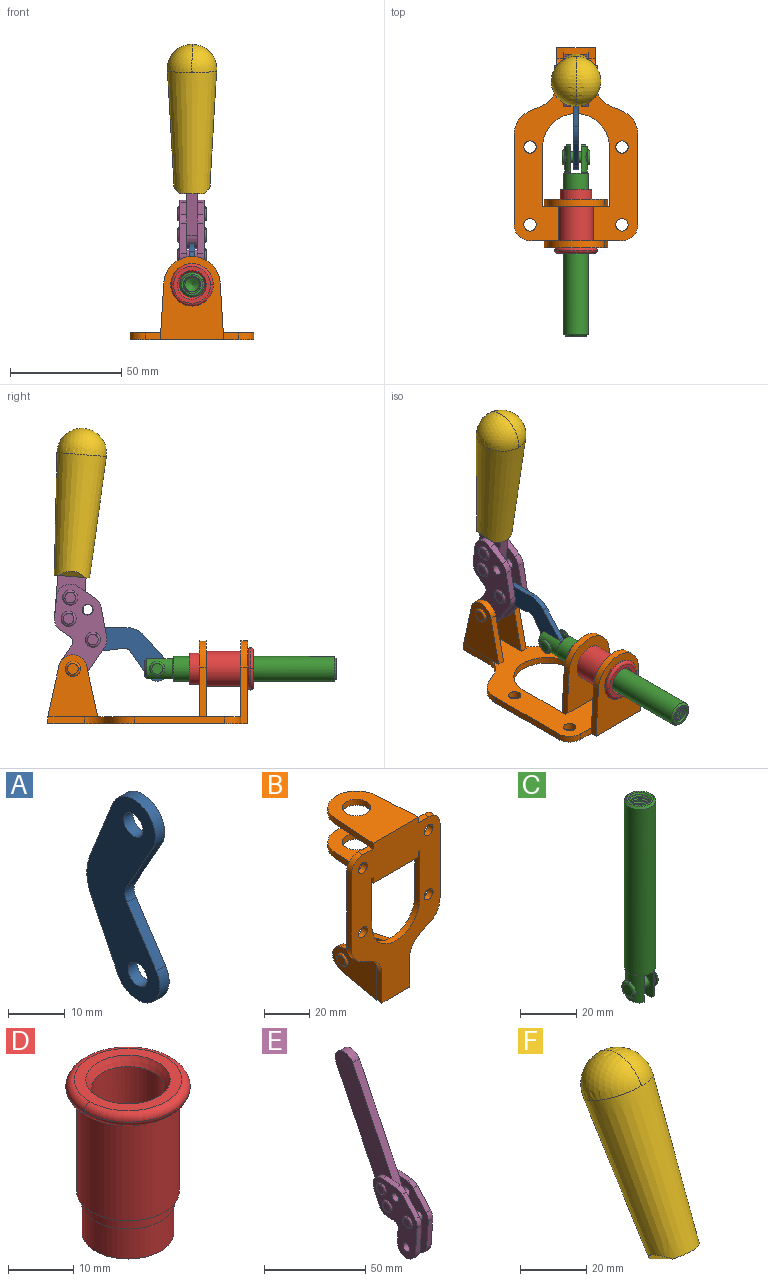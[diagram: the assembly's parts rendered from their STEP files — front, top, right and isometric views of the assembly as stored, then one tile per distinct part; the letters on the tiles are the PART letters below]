
ASSEMBLY  parts=6 mates=6
PART A: 12 faces, bbox 2.3x18.2x42.8 mm
  f0: cylinder r=2.4mm len=4.8mm, axis (1,0,0), area 34.9mm2, adj f4,f11
  f1: cylinder r=10.41mm len=8.47mm, axis (1,0,0), area 20.2mm2, adj f4,f9,f10,f11
  f2: cylinder r=3.05mm len=3.16mm, axis (1,0,0), area 7.7mm2, adj f4,f6,f7,f11
  f3: cylinder r=2.4mm len=4.8mm, axis (1,0,0), area 34.9mm2, adj f4,f11
  f4: plane 42.81x18.23mm, normal (-1,0,0), area 414.1mm2, adj f0,f1,f2,f3,f5,f6,f7,f8
  f5: cylinder r=5.54mm len=10.67mm, axis (1,0,0), area 41.8mm2, adj f4,f6,f10,f11
  f6: plane 11.66x6.53mm, normal (0,-0.87,-0.49), area 30.9mm2, adj f2,f4,f5,f11
  f7: plane 11.17x7.33mm, normal (0,-0.84,0.55), area 30.9mm2, adj f2,f4,f8,f11
  f8: cylinder r=5.54mm len=10.51mm, axis (1,0,0), area 41.8mm2, adj f4,f7,f9,f11
  f9: plane 13.67x6.67mm, normal (0,0.9,-0.44), area 35.1mm2, adj f1,f4,f8,f11
  f10: plane 14.1x5.7mm, normal (0,0.93,0.37), area 35.1mm2, adj f1,f4,f5,f11
  f11: plane 42.81x18.23mm, normal (1,0,0), area 414.1mm2, adj f0,f1,f2,f3,f5,f6,f7,f8
PART B: 55 faces, bbox 55.7x37.4x89.8 mm
  f0: torus R=2.41mm, axis (-1,0,0), area 15mm2, adj f11,f15,f25
  f1: torus R=2.41mm, axis (-1,0,0), area 15mm2, adj f10,f12,f22
  f2: cylinder r=2.78mm len=5.56mm, axis (0,-1,0), area 54.2mm2, adj f30,f54
  f3: cylinder r=14.99mm len=29.97mm, axis (0,-1,0), area 145.9mm2, adj f30,f49,f53,f54
  f4: cylinder r=2.78mm len=5.56mm, axis (0,-1,0), area 54.2mm2, adj f30,f54
  f5: cylinder r=2.78mm len=5.56mm, axis (0,-1,0), area 54.2mm2, adj f30,f54
  f6: cylinder r=2.78mm len=5.56mm, axis (0,-1,0), area 54.2mm2, adj f30,f54
  f7: cylinder r=6.35mm len=12.7mm, axis (0,0,1), area 123.6mm2, adj f27,f51
  f8: cylinder r=6.35mm len=12.7mm, axis (0,0,-1), area 124.7mm2, adj f21,f35
  f9: cylinder r=2.41mm len=11.18mm, axis (-1,0,0), area 169.4mm2, adj f16,f19
  f10: plane 4.83x4.83mm, normal (1,0,0), area 18.3mm2, adj f1,f12
  f11: plane 4.83x4.83mm, normal (-1,0,0), area 18.3mm2, adj f0,f15
  f12: torus R=2.41mm, axis (-1,0,0), area 15mm2, adj f1,f10,f22
  f13: cylinder r=6.35mm len=12.41mm, axis (1,0,0), area 53.4mm2, adj f18,f19,f22,f23
  f14: cylinder r=6.35mm len=12.41mm, axis (-1,0,0), area 53.4mm2, adj f16,f17,f24,f25
  f15: torus R=2.41mm, axis (-1,0,0), area 15mm2, adj f0,f11,f25
  f16: plane 27.86x22.35mm, normal (1,0,0), area 425.4mm2, adj f9,f14,f17,f24,f30
  f17: plane 22.86x4.97mm, normal (0,0.21,0.98), area 72.5mm2, adj f14,f16,f25,f30
  f18: plane 22.86x4.97mm, normal (0,0.21,0.98), area 72.5mm2, adj f13,f19,f22,f30
  f19: plane 27.86x22.35mm, normal (-1,0,0), area 425.4mm2, adj f9,f13,f18,f23,f30
  f20: cylinder r=12.7mm len=25.35mm, axis (0,0,-1), area 119.8mm2, adj f21,f34,f35,f36
  f21: plane 34.21x28.07mm, normal (0,0,-1), area 702.4mm2, adj f8,f20,f30,f34,f36
  f22: plane 27.96x22.45mm, normal (1,0,0), area 407.2mm2, adj f1,f12,f13,f18,f23,f30,f42,f43
  f23: plane 22.86x4.97mm, normal (0,0.21,-0.98), area 72.5mm2, adj f13,f19,f22,f44
  f24: plane 22.86x4.97mm, normal (0,0.21,-0.98), area 72.5mm2, adj f14,f16,f25,f44
  f25: plane 27.86x22.35mm, normal (-1,0,0), area 407.1mm2, adj f0,f14,f15,f17,f24,f30,f45,f46
  f26: plane 3.1x0.95mm, normal (0,0,-1), area 2.7mm2, adj f30,f49,f50,f54
  f27: plane 34.21x28.07mm, normal (0,0,1), area 702.4mm2, adj f7,f28,f30,f50,f52
  f28: cylinder r=12.7mm len=25.35mm, axis (0,0,1), area 118.8mm2, adj f27,f50,f51,f52
  f29: plane 3.1x0.95mm, normal (0,0,-1), area 2.7mm2, adj f30,f52,f53,f54
  f30: plane 86.54x55.63mm, normal (0,1,0), area 2362.9mm2, adj f2,f3,f4,f5,f6,f16,f17,f18
  f31: plane 40.56x3.1mm, normal (-1,0,0), area 125.7mm2, adj f30,f32,f48,f54
  f32: cylinder r=7.11mm len=7.11mm, axis (0,-1,0), area 34.6mm2, adj f30,f31,f33,f54
  f33: plane 6.67x3.1mm, normal (0,0,1), area 20.4mm2, adj f30,f32,f34,f54
  f34: plane 25.39x3.13mm, normal (-1,0.06,0), area 79.5mm2, adj f20,f21,f33,f35,f54
  f35: plane 37.31x28.45mm, normal (0,0,1), area 789.9mm2, adj f8,f20,f34,f36,f54
  f36: plane 25.39x3.13mm, normal (1,0.06,0), area 79.5mm2, adj f20,f21,f35,f37,f54
  f37: plane 6.67x3.1mm, normal (0,0,1), area 20.4mm2, adj f30,f36,f38,f54
  f38: cylinder r=7.11mm len=7.11mm, axis (0,-1,0), area 34.6mm2, adj f30,f37,f39,f54
  f39: plane 40.56x3.1mm, normal (1,0,0), area 125.7mm2, adj f30,f38,f40,f54
  f40: cylinder r=11.18mm len=10.16mm, axis (0,-1,0), area 39.5mm2, adj f30,f39,f41,f54
  f41: plane 6.09x3.1mm, normal (0.42,0,-0.91), area 20.8mm2, adj f30,f40,f42,f54
  f42: cylinder r=11.18mm len=9.41mm, axis (0,-1,0), area 37.2mm2, adj f22,f30,f41,f43,f54
  f43: plane 16.5x3.1mm, normal (1,0,0), area 51.1mm2, adj f22,f42,f44,f54
  f44: plane 17.37x3.1mm, normal (0,0,-1), area 53.8mm2, adj f23,f24,f30,f43,f45,f54
  f45: plane 16.5x3.1mm, normal (-1,0,0), area 51.1mm2, adj f25,f44,f46,f54
  f46: cylinder r=11.18mm len=9.41mm, axis (0,-1,0), area 37.2mm2, adj f25,f30,f45,f47,f54
  f47: plane 6.09x3.1mm, normal (-0.42,0,-0.91), area 20.8mm2, adj f30,f46,f48,f54
  f48: cylinder r=11.18mm len=10.16mm, axis (0,-1,0), area 39.5mm2, adj f30,f31,f47,f54
  f49: plane 26.54x3.1mm, normal (-1,0,0), area 82.3mm2, adj f3,f26,f30,f54
  f50: plane 25.39x3.1mm, normal (1,0.06,0), area 78.8mm2, adj f26,f27,f28,f51,f54
  f51: plane 37.31x28.45mm, normal (0,0,-1), area 789.9mm2, adj f7,f28,f50,f52,f54
  f52: plane 25.39x3.1mm, normal (-1,0.06,0), area 78.8mm2, adj f27,f28,f29,f51,f54
  f53: plane 26.54x3.1mm, normal (1,0,0), area 82.3mm2, adj f3,f29,f30,f54
  f54: plane 89.66x55.63mm, normal (0,-1,0), area 2678.5mm2, adj f2,f3,f4,f5,f6,f26,f29,f31
PART C: 48 faces, bbox 12.6x11.1x86.1 mm
  f0: torus R=2.41mm, axis (-1,0,0), area 15mm2, adj f30,f32,f34
  f1: torus R=2.41mm, axis (-1,0,0), area 15mm2, adj f29,f31,f33
  f2: cylinder r=5.54mm len=72.39mm, axis (0,0,1), area 2518.5mm2, adj f3,f4,f42,f43
  f3: cone r=5.54mm half-angle=45deg, axis (0,0,1), area 7.6mm2, adj f2,f5,f41
  f4: cone r=5.54mm half-angle=45deg, axis (0,0,-1), area 34.9mm2, adj f2,f39
  f5: cylinder r=5.08mm len=11.48mm, axis (0,0,1), area 108.3mm2, adj f3,f7,f8,f41
  f6: cylinder r=2.41mm len=4.83mm, axis (-1,0,0), area 71.2mm2, adj f40,f41
  f7: cylinder r=2.41mm len=4.83mm, axis (-1,0,0), area 7.6mm2, adj f5,f34
  f8: cone r=5.08mm half-angle=45deg, axis (0,0,1), area 10.6mm2, adj f5,f37,f41
  f9: cone r=3.98mm half-angle=45deg, axis (0,0,1), area 17.6mm2, adj f27,f39,f45,f46,f47
  f10: cylinder r=2.41mm len=4.83mm, axis (-1,0,0), area 7.6mm2, adj f33,f38
  f11: cylinder r=3.2mm len=6.4mm, axis (0,0,1), area 78.4mm2, adj f12,f28,f44,f45,f47
  f12: cylinder r=3.2mm len=6.4mm, axis (0,0,1), area 10.5mm2, adj f11,f13,f45,f47
  f13: cylinder r=3.2mm len=6.4mm, axis (0,0,1), area 10.5mm2, adj f12,f14,f45,f47
  f14: cylinder r=3.2mm len=6.4mm, axis (0,0,1), area 10.5mm2, adj f13,f15,f45,f47
  f15: cylinder r=3.2mm len=6.4mm, axis (0,0,1), area 10.5mm2, adj f14,f16,f45,f47
  f16: cylinder r=3.2mm len=6.4mm, axis (0,0,1), area 10.5mm2, adj f15,f17,f45,f47
  f17: cylinder r=3.2mm len=6.4mm, axis (0,0,1), area 10.5mm2, adj f16,f18,f45,f47
  f18: cylinder r=3.2mm len=6.4mm, axis (0,0,1), area 10.5mm2, adj f17,f19,f45,f47
  f19: cylinder r=3.2mm len=6.4mm, axis (0,0,1), area 10.5mm2, adj f18,f20,f45,f47
  f20: cylinder r=3.2mm len=6.4mm, axis (0,0,1), area 10.5mm2, adj f19,f21,f45,f47
  f21: cylinder r=3.2mm len=6.4mm, axis (0,0,1), area 10.5mm2, adj f20,f22,f45,f47
  f22: cylinder r=3.2mm len=6.4mm, axis (0,0,1), area 10.5mm2, adj f21,f23,f45,f47
  f23: cylinder r=3.2mm len=6.4mm, axis (0,0,1), area 10.5mm2, adj f22,f24,f45,f47
  f24: cylinder r=3.2mm len=6.4mm, axis (0,0,1), area 10.5mm2, adj f23,f25,f45,f47
  f25: cylinder r=3.2mm len=6.4mm, axis (0,0,1), area 10.5mm2, adj f24,f26,f45,f47
  f26: cylinder r=3.2mm len=6.4mm, axis (0,0,1), area 10.5mm2, adj f25,f27,f45,f47
  f27: cylinder r=3.2mm len=6.4mm, axis (0,0,1), area 7.4mm2, adj f9,f26,f45,f47
  f28: cone r=3.2mm half-angle=60deg, axis (0,0,1), area 37.2mm2, adj f11
  f29: plane 4.83x4.83mm, normal (-1,0,0), area 18.3mm2, adj f1,f31
  f30: plane 4.83x4.83mm, normal (1,0,0), area 18.3mm2, adj f0,f32
  f31: torus R=2.41mm, axis (-1,0,0), area 15mm2, adj f1,f29,f33
  f32: torus R=2.41mm, axis (-1,0,0), area 15mm2, adj f0,f30,f34
  f33: plane 6.83x6.83mm, normal (1,0,0), area 18.3mm2, adj f1,f10,f31
  f34: plane 6.83x6.83mm, normal (-1,0,0), area 18.3mm2, adj f0,f7,f32
  f35: cone r=5.08mm half-angle=45deg, axis (0,0,1), area 10.6mm2, adj f36,f38,f40
  f36: plane 7.25x1.97mm, normal (0,0,-1), area 10mm2, adj f35,f40
  f37: plane 7.25x1.97mm, normal (0,0,-1), area 10mm2, adj f8,f41
  f38: cylinder r=5.08mm len=11.48mm, axis (0,0,1), area 108.3mm2, adj f10,f35,f40,f42
  f39: plane 9.55x9.55mm, normal (0,0,1), area 22mm2, adj f4,f9
  f40: plane 12.76x10.09mm, normal (1,0,0), area 95.7mm2, adj f6,f35,f36,f38,f42,f43
  f41: plane 12.76x10.09mm, normal (-1,0,0), area 95.7mm2, adj f3,f5,f6,f8,f37,f43
  f42: cone r=5.54mm half-angle=45deg, axis (0,0,1), area 7.6mm2, adj f2,f38,f40
  f43: plane 11.07x4.7mm, normal (0,0,-1), area 50.4mm2, adj f2,f40,f41
  f44: plane 0.89x0.62mm, normal (-1,0,0), area 0.3mm2, adj f11,f45,f46,f47
  f45: bspline ~24.8x7.63mm, area 266.6mm2, adj f9,f11,f12,f13,f14,f15,f16,f17
  f46: bspline ~24.87x7.63mm, area 73.6mm2, adj f9,f44,f45,f47
  f47: bspline ~24.98x7.63mm, area 272.5mm2, adj f9,f11,f12,f13,f14,f15,f16,f17
PART D: 15 faces, bbox 20.6x20.6x28.7 mm
  f0: torus R=8.26mm, axis (0,0,1), area 56.8mm2, adj f1,f10,f12
  f1: torus R=8.26mm, axis (0,0,1), area 56.8mm2, adj f0,f6,f13
  f2: cylinder r=5.59mm len=25.91mm, axis (0,0,1), area 909.6mm2, adj f3,f4
  f3: cone r=6.86mm half-angle=45deg, axis (0,0,-1), area 70.2mm2, adj f2,f14
  f4: cone r=6.47mm half-angle=30deg, axis (0,0,1), area 66.7mm2, adj f2,f13
  f5: cylinder r=7.04mm len=14.07mm, axis (0,0,1), area 252.6mm2, adj f11,f14
  f6: torus R=8.26mm, axis (0,0,1), area 56.8mm2, adj f1,f12,f13
  f7: cylinder r=7.16mm len=14.33mm, axis (0,0,1), area 91.5mm2, adj f9,f11
  f8: cylinder r=7.86mm len=18.42mm, axis (0,0,1), area 909.6mm2, adj f9,f10
  f9: plane 15.72x15.72mm, normal (0,0,-1), area 33mm2, adj f7,f8
  f10: plane 16.51x16.51mm, normal (0,0,-1), area 19.9mm2, adj f0,f8,f12
  f11: plane 14.33x14.33mm, normal (0,0,-1), area 5.7mm2, adj f5,f7
  f12: torus R=8.26mm, axis (0,0,1), area 56.8mm2, adj f0,f6,f10
  f13: plane 16.51x16.51mm, normal (0,0,1), area 82.7mm2, adj f1,f4,f6
  f14: plane 14.07x14.07mm, normal (0,0,-1), area 7.8mm2, adj f3,f5
PART E: 59 faces, bbox 12.9x60.2x99.6 mm
  f0: torus R=2.39mm, axis (-1,0,0), area 14.9mm2, adj f20,f43,f51
  f1: torus R=2.39mm, axis (-1,0,0), area 14.9mm2, adj f19,f42,f51
  f2: torus R=2.39mm, axis (-1,0,0), area 14.9mm2, adj f18,f35,f51
  f3: torus R=2.39mm, axis (-1,0,0), area 14.9mm2, adj f14,f17,f23
  f4: torus R=2.39mm, axis (-1,0,0), area 14.9mm2, adj f13,f16,f23
  f5: torus R=2.39mm, axis (-1,0,0), area 14.9mm2, adj f12,f15,f23
  f6: cylinder r=2.39mm len=4.78mm, axis (1,0,0), area 46.5mm2, adj f48,f50,f51
  f7: cylinder r=2.39mm len=4.78mm, axis (1,0,0), area 46.5mm2, adj f50,f51
  f8: cylinder r=6.35mm len=12.68mm, axis (1,0,0), area 61.8mm2, adj f38,f39,f50,f51
  f9: cylinder r=2.39mm len=4.78mm, axis (-1,0,0), area 70.5mm2, adj f46,f50
  f10: cylinder r=2.39mm len=4.78mm, axis (-1,0,0), area 46.5mm2, adj f23,f45,f46
  f11: cylinder r=2.39mm len=4.78mm, axis (-1,0,0), area 46.5mm2, adj f23,f46
  f12: plane 4.78x4.78mm, normal (1,0,0), area 17.9mm2, adj f5,f15
  f13: plane 4.78x4.78mm, normal (1,0,0), area 17.9mm2, adj f4,f16
  f14: plane 4.78x4.78mm, normal (1,0,0), area 17.9mm2, adj f3,f17
  f15: torus R=2.39mm, axis (-1,0,0), area 14.9mm2, adj f5,f12,f23
  f16: torus R=2.39mm, axis (-1,0,0), area 14.9mm2, adj f4,f13,f23
  f17: torus R=2.39mm, axis (-1,0,0), area 14.9mm2, adj f3,f14,f23
  f18: plane 4.78x4.78mm, normal (-1,0,0), area 17.9mm2, adj f2,f35
  f19: plane 4.78x4.78mm, normal (-1,0,0), area 17.9mm2, adj f1,f42
  f20: plane 4.78x4.78mm, normal (-1,0,0), area 17.9mm2, adj f0,f43
  f21: plane 2.26x0.2mm, normal (1,0,0), area 0.2mm2, adj f31,f44
  f22: plane 2.26x0.2mm, normal (-1,0,0), area 0.2mm2, adj f41,f44
  f23: plane 39.37x30.77mm, normal (1,0,0), area 565.5mm2, adj f3,f4,f5,f10,f11,f15,f16,f17
  f24: cylinder r=6.1mm len=4.15mm, axis (-1,0,0), area 14.7mm2, adj f23,f25,f32,f46
  f25: plane 10.25x9.01mm, normal (0,-0.75,0.66), area 42.3mm2, adj f23,f24,f26,f46
  f26: cylinder r=6.35mm len=4.64mm, axis (-1,0,0), area 15.6mm2, adj f23,f25,f27,f46
  f27: plane 15.84x3.1mm, normal (0,-1,-0.07), area 49.2mm2, adj f23,f26,f28,f46
  f28: cylinder r=6.35mm len=12.68mm, axis (-1,0,0), area 61.8mm2, adj f23,f27,f29,f46
  f29: plane 8.11x3.1mm, normal (0,1,0.07), area 25.2mm2, adj f23,f28,f30,f46
  f30: cylinder r=3.05mm len=3.25mm, axis (-1,0,0), area 14.8mm2, adj f23,f29,f31,f46
  f31: plane 5.99x3.1mm, normal (0,0.07,-1), area 18.6mm2, adj f21,f23,f30,f44,f46
  f32: plane 9.5x3.1mm, normal (0,-0.07,1), area 29.5mm2, adj f23,f24,f33,f46,f47
  f33: cylinder r=6.1mm len=8.63mm, axis (-1,0,0), area 39.1mm2, adj f23,f32,f34,f47
  f34: plane 8.65x3.96mm, normal (0,0.91,-0.42), area 29.5mm2, adj f23,f33,f44,f47
  f35: torus R=2.39mm, axis (-1,0,0), area 14.9mm2, adj f2,f18,f51
  f36: plane 10.25x9.01mm, normal (0,-0.75,0.66), area 42.3mm2, adj f37,f49,f50,f51
  f37: cylinder r=6.35mm len=4.64mm, axis (1,0,0), area 15.6mm2, adj f36,f38,f50,f51
  f38: plane 15.84x3.1mm, normal (0,-1,-0.07), area 49.2mm2, adj f8,f37,f50,f51
  f39: plane 8.11x3.1mm, normal (0,1,0.07), area 25.2mm2, adj f8,f40,f50,f51
  f40: cylinder r=3.05mm len=3.25mm, axis (1,0,0), area 14.8mm2, adj f39,f41,f50,f51
  f41: plane 5.99x3.1mm, normal (0,0.07,-1), area 18.6mm2, adj f22,f40,f44,f50,f51
  f42: torus R=2.39mm, axis (-1,0,0), area 14.9mm2, adj f1,f19,f51
  f43: torus R=2.39mm, axis (-1,0,0), area 14.9mm2, adj f0,f20,f51
  f44: cylinder r=6.35mm len=12.12mm, axis (-1,0,0), area 128.9mm2, adj f21,f22,f23,f31,f34,f41,f46,f47
  f45: plane 2.65x1.35mm, normal (1,0,0), area 1mm2, adj f10,f55
  f46: plane 39.08x20.42mm, normal (-1,0,0), area 412.5mm2, adj f9,f10,f11,f24,f25,f26,f27,f28
  f47: plane 77.62x39.82mm, normal (1,0,0), area 850mm2, adj f32,f33,f34,f44,f53,f54,f55
  f48: plane 2.65x1.35mm, normal (-1,0,0), area 1mm2, adj f6,f55
  f49: cylinder r=6.1mm len=4.15mm, axis (1,0,0), area 14.7mm2, adj f36,f50,f51,f56
  f50: plane 39.08x20.42mm, normal (1,0,0), area 412.5mm2, adj f6,f7,f8,f9,f36,f37,f38,f39
  f51: plane 39.37x30.77mm, normal (-1,0,0), area 565.5mm2, adj f0,f1,f2,f6,f7,f8,f35,f36
  f52: plane 8.65x3.96mm, normal (0,0.91,-0.42), area 29.5mm2, adj f44,f51,f57,f58
  f53: plane 68.49x33.4mm, normal (0,0.9,-0.44), area 358.1mm2, adj f44,f47,f54,f58
  f54: cylinder r=6.35mm len=12.06mm, axis (1,0,0), area 93.7mm2, adj f47,f53,f55,f58
  f55: plane 68.49x33.4mm, normal (0,-0.9,0.44), area 358.1mm2, adj f44,f45,f46,f47,f48,f50,f54,f58
  f56: plane 9.5x3.1mm, normal (0,-0.07,1), area 29.5mm2, adj f49,f50,f51,f57,f58
  f57: cylinder r=6.1mm len=8.63mm, axis (1,0,0), area 39.1mm2, adj f51,f52,f56,f58
  f58: plane 77.62x39.82mm, normal (-1,0,0), area 850mm2, adj f44,f52,f53,f54,f55,f56,f57
PART F: 11 faces, bbox 22.3x42.6x64.5 mm
  f0: sphere r=11.13mm, area 411.4mm2, adj f1,f8
  f1: cone r=11.11mm half-angle=3.3deg, axis (0,0.44,0.9), area 3251.8mm2, adj f0,f7,f8,f9,f10
  f2: cylinder r=6.16mm len=11.7mm, axis (1,0,0), area 89.5mm2, adj f3,f4,f5,f6
  f3: plane 60.23x36.75mm, normal (-1,0,0), area 763.6mm2, adj f2,f4,f6,f10
  f4: plane 51.37x25.05mm, normal (0,0.9,-0.44), area 264.2mm2, adj f2,f3,f5,f10
  f5: plane 60.23x36.75mm, normal (1,0,0), area 763.6mm2, adj f2,f4,f6,f10
  f6: plane 51.37x25.05mm, normal (0,-0.9,0.44), area 264.2mm2, adj f2,f3,f5,f10
  f7: plane 9.95x5.95mm, normal (0.71,-0.31,-0.64), area 25.8mm2, adj f1,f10
  f8: sphere r=11.13mm, area 411.4mm2, adj f0,f1
  f9: plane 9.95x5.95mm, normal (-0.71,-0.31,-0.64), area 25.8mm2, adj f1,f10
  f10: plane 14.27x11.38mm, normal (0,-0.44,-0.9), area 106.7mm2, adj f1,f3,f4,f5,f6,f7,f9
PLACE A rot(axis=(1,0,0),116.3deg) t=(0,28.08,9.41)mm
PLACE B rot(axis=(1,0,0),90deg) t=(0,9.14,0)mm fixed
PLACE C rot(axis=(1,0,0),90deg) t=(0,18.77,0)mm
PLACE D rot(axis=(1,0,0),90deg) t=(0,9.14,0)mm
PLACE E rot(axis=(1,0,0),30.5deg) t=(0,3.73,39.75)mm
PLACE F rot(axis=(1,0,0),30.5deg) t=(0,3.73,39.75)mm
MATE fastened F.f2 <-> E.f54  axis (-1,0,0) through (0,37.08,123.02)mm
MATE revolute A.f5 <-> C.f6  axis (1,0,0) through (0,3.3,24.61)mm
MATE revolute E.f7 <-> B.f0  axis (1,0,0) through (0,41.23,24.61)mm
MATE slider D.f2 <-> C.f2  axis (0,-1,0) through (0,-39.79,24.61)mm
MATE revolute A.f3 <-> E.f4  axis (1,0,0) through (0,32.23,37.69)mm
MATE fastened D.f2 <-> B.f7  axis (0,1,0) through (0,-37.25,24.61)mm
